# Revit family: Weitspannkabelleiter - WKLG 1150 FT, FS, A2, A4.
name_source: partatom
category: Generic Models
revit_build: Autodesk Revit 2017 (Build: 20190508_0315(x64)
units: mm (PartAtom-declared; Revit-internal decimal feet)

## family parameters
Always vertical = Yes
Can host rebar = No
Cut with Voids When Loaded = No
Part Type = Normal
Room Calculation Point = No
Round Connector Dimension = Use Diameter
Shared = No
Work Plane-Based = No

## types (5) — shared parameters
Cut's number = 80
Cut's number 2 = 79
Cut's number 3 = 20
Cut's number 4 = 19
Cut's number 5 = 2
Cut's space = 75 mm
Cut's space 2 = 300 mm
Cut's space 3 = 3000 mm  [stored 9.84252 ft]
Height = 110 mm  [stored 0.360892 ft]
Height 1 = 2 mm  [stored 0.00656168 ft]
Length = 6000 mm  [stored 19.685 ft]
Manufacturer = OBO Bettermann
URL = http://www.obo-bettermann.com
Width = 35 mm
Width 1 = 500 mm  [stored 1.64042 ft]
Width 2 = 250 mm  [stored 0.82021 ft]

## per-type parameters (varying)
| type | GTIN | Manufacturer Art.No. | Material |
| WKLG 1150 FT | 4012196883516 | 6311071 | Hot-dip galvanised |
| WKLG 1150 FS | 4012196883219 | 6311020 | Strip-galvanised |
| WKLG 1150 A2 | 4012195037316 | 6311214 | Stainless steel, A2 |
| WKLG 1150 A4 | 4012195866329 | 6311231 | Stainless steel, A4 |
| WKLG 1150 FT SO | 4012195859277 | 7189020 | Hot-dip galvanised 85 µm |

note: column(s) folded — value = type name in every type: Article Type

note: [stored X ft] marks values corroborated as IEEE doubles in the binary element streams (Revit-internal decimal feet)

## geometry (parser evidence)
native form markers: Sweep x3
no freeform markers — native parametric forms only
